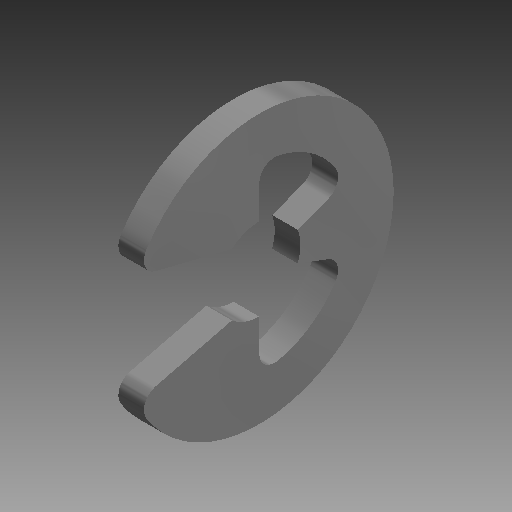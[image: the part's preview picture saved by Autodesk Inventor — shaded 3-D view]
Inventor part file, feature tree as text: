
AUTODESK INVENTOR PART (.ipt)
format: ipt  version: 2019 (Build 230136000, 136)  size: 91,136 bytes
history: native  units: mm (DEFAULTED — no unit token found)
features: fillet x1
ambient origin geometry x8: Origin, YZ Plane, XZ Plane, XY Plane, X Axis, Y Axis, Z Axis, Center Point
bodies: Solid1 (feature_tree)
feature tree (1):
  fillet  "Fillet1"  [1 undecoded]
note: 1 required parameter value undecoded (feature->parameter linkage not recoverable at this tier; creation-order binding heuristic only, values carry confidence <= 0.55)
